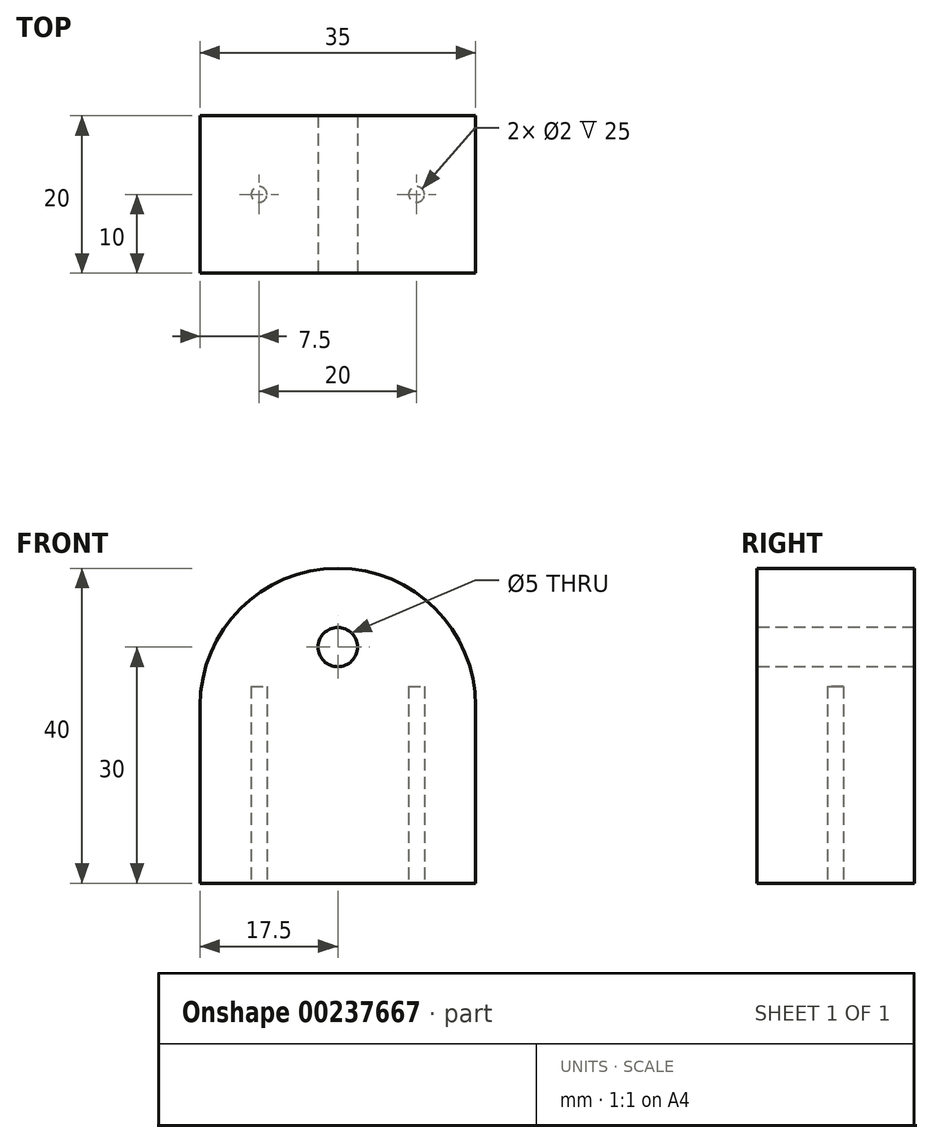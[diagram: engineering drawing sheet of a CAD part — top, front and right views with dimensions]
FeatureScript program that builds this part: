
annotation { "Feature Type Name" : "Feature", "Feature Type Description" : "" }
export const myFeature = defineFeature(function(context is Context, id is Id, definition is map)
    precondition{}
    {
        {
            var Q0;
            Q0=qCreatedBy(makeId("Top.planeOp"),FACE);
            var sketch = newSketch(context, id + "F0", { "sketchPlane" : qUnion([Q0])});
            skLineSegment(sketch, "E0", {"start": v(0, 10) * mm, "end": v(17.5, 10) * mm});
            skLineSegment(sketch, "E1", {"start": v(17.5, 10) * mm, "end": v(17.5, -10) * mm});
            skLineSegment(sketch, "E2", {"start": v(17.5, -10) * mm, "end": v(-17.5, -10) * mm});
            skLineSegment(sketch, "E3", {"start": v(-17.5, -10) * mm, "end": v(-17.5, 10) * mm});
            skLineSegment(sketch, "E4", {"start": v(-17.5, 10) * mm, "end": v(0, 10) * mm});
            skSolve(sketch);
        }
        {
            var Q0;
            Q0 = qSketchRegion(id + "F0", true);
            extrude(context, id + "F1", {"entities" : qUnion([Q0]), "depth" : 40 * mm});
        }
        {
            var Q0;
            Q0=makeQuery(id+"F1.opExtrude","CAP_EDGE",EDGE,{"disambiguationData":[OSD([sQuery(id+"F0.wireOp",EDGE,"E1")])],"isStart":false});
            var Q1;
            Q1=makeQuery(id+"F1.opExtrude","CAP_EDGE",EDGE,{"disambiguationData":[OSD([sQuery(id+"F0.wireOp",EDGE,"E3")])],"isStart":false});
            fillet(context, id + "F2", {"entities" : qUnion([Q0, Q1]), "radius" : 17.5 * mm, "tangentPropagation" : true, "allowEdgeOverflow" : false});
        }
        {
            var Q0;
            Q0=makeQuery(id+"F1.opExtrude","SWEPT_FACE",FACE,{"disambiguationData":[OSD([sQuery(id+"F0.wireOp",EDGE,"E2")])]});
            var sketch = newSketch(context, id + "F3", { "sketchPlane" : qUnion([Q0])});
            skPoint(sketch, "E5.endSnap0", {"position": v(0, 0) * mm});
            skCircle(sketch, "E6", {"center": v(0, 30) * mm, "radius": 2.5 * mm});
            skSolve(sketch);
        }
        {
            var Q0;
            Q0 = qSketchRegion(id + "F3", true);
            extrude(context, id + "F4", {"entities" : qUnion([Q0]), "operationType" : NewBodyOperationType.REMOVE, "oppositeDirection" : true, "depth" : 25 * mm});
        }
        {
            var Q0;
            Q0=makeQuery(id+"F1.opExtrude","CAP_FACE",FACE,{"disambiguationData":[OSD([sQuery(id+"F0.wireOp",EDGE,"E0"),sQuery(id+"F0.wireOp",EDGE,"E1"),sQuery(id+"F0.wireOp",EDGE,"E2"),sQuery(id+"F0.wireOp",EDGE,"E3"),sQuery(id+"F0.wireOp",EDGE,"E4")])],"isStart":true});
            var sketch = newSketch(context, id + "F5", { "sketchPlane" : qUnion([Q0])});
            skCircle(sketch, "E7", {"center": v(10, 0) * mm, "radius": 1 * mm});
            skCircle(sketch, "E8", {"center": v(-10, 0) * mm, "radius": 1 * mm});
            skSolve(sketch);
        }
        {
            var Q0;
            Q0 = qSketchRegion(id + "F5", true);
            extrude(context, id + "F6", {"entities" : qUnion([Q0]), "operationType" : NewBodyOperationType.REMOVE, "oppositeDirection" : true, "depth" : 25 * mm});
        }
    });
